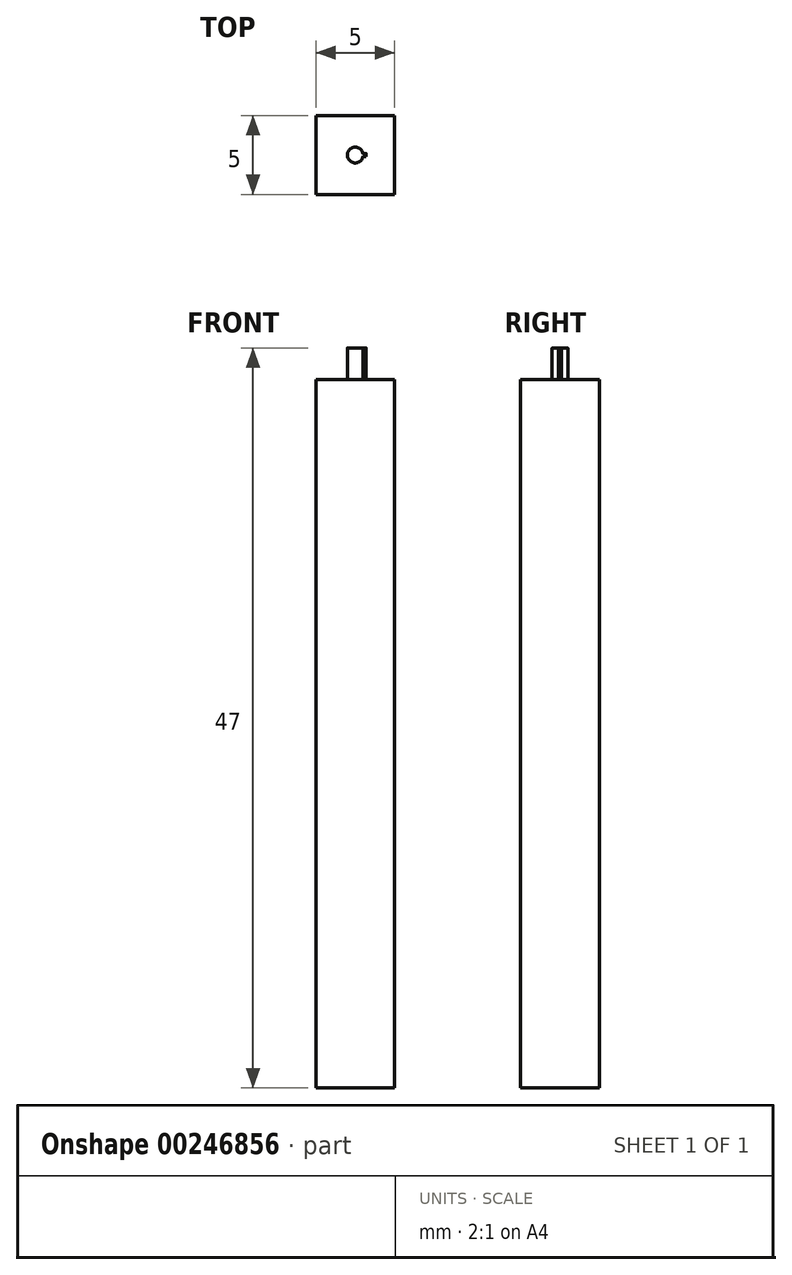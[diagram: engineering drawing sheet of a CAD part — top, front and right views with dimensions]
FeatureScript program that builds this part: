
annotation { "Feature Type Name" : "Feature", "Feature Type Description" : "" }
export const myFeature = defineFeature(function(context is Context, id is Id, definition is map)
    precondition{}
    {
        {
            var Q0;
            Q0=qCreatedBy(makeId("Front.planeOp"),FACE);
            var sketch = newSketch(context, id + "F0", { "sketchPlane" : qUnion([Q0])});
            skLineSegment(sketch, "E0", {"start": v(-2.5, 0) * mm, "end": v(-2.5, 45) * mm});
            skLineSegment(sketch, "E1", {"start": v(-2.5, 45) * mm, "end": v(0, 45) * mm});
            skLineSegment(sketch, "E2.MirrorCS", {"start": v(2.5, 45) * mm, "end": v(0, 45) * mm});
            skLineSegment(sketch, "E3.MirrorCS", {"start": v(2.5, 0) * mm, "end": v(2.5, 45) * mm});
            skLineSegment(sketch, "E4", {"start": v(-2.5, 0) * mm, "end": v(2.5, 0) * mm});
            skLineSegment(sketch, "E5", {"start": v(-2.5, 0) * mm, "end": v(-3, 0) * mm});
            skLineSegment(sketch, "E6.MirrorCS", {"start": v(2.5, 0) * mm, "end": v(3, 0) * mm});
            skSolve(sketch);
        }
        {
            var Q0;
            {var subQ6=sQuery(id+"F0.wireOp",EDGE,"E0");Q0=makeQuery(id+"F0.imprint","IMPRINT",FACE,{"disambiguationData":[TD([[makeQuery(id+"F0.imprint","IMPRINT",EDGE,{"derivedFrom":subQ6}),-1.0]])]});}
            extrude(context, id + "F1", {"entities" : qUnion([Q0]), "depth" : 5 * mm});
        }
        {
            var Q0;
            Q0=makeQuery(id+"F1.opExtrude","SWEPT_FACE",FACE,{"disambiguationData":[OSD([sQuery(id+"F0.wireOp",EDGE,"E1"),sQuery(id+"F0.wireOp",EDGE,"E2.MirrorCS")])]});
            var sketch = newSketch(context, id + "F2", { "sketchPlane" : qUnion([Q0])});
            skCircle(sketch, "E7", {"center": v(0, -2.5) * mm, "radius": 0.5 * mm});
            skPoint(sketch, "E7.centerSnap0", {"position": v(-2.5, -2.5) * mm});
            skLineSegment(sketch, "E8", {"start": v(0.49, -2.4) * mm, "end": v(0.69, -2.4) * mm});
            skLineSegment(sketch, "E9", {"start": v(0.69, -2.4) * mm, "end": v(0.69, -2.5) * mm});
            skLineSegment(sketch, "E10", {"start": v(0.69, -2.5) * mm, "end": v(0.69, -2.6) * mm});
            skLineSegment(sketch, "E11", {"start": v(0.69, -2.6) * mm, "end": v(0.49, -2.6) * mm});
            skSolve(sketch);
        }
        {
            var Q0;
            Q0=makeQuery(id+"F2.imprint","IMPRINT",FACE,{"disambiguationData":[TD([[makeQuery(id+"F2.imprint","IMPRINT",EDGE,{"derivedFrom":sQuery(id+"F2.wireOp",EDGE,"E7")}),1.0]])]});
            extrude(context, id + "F3", {"entities" : qUnion([Q0]), "operationType" : NewBodyOperationType.ADD, "depth" : 2 * mm});
        }
        {
            var Q0;
            {var subQ0=sQuery(id+"F2.wireOp",EDGE,"E8");Q0=makeQuery(id+"F2.imprint","IMPRINT",FACE,{"disambiguationData":[TD([[makeQuery(id+"F2.imprint","IMPRINT",EDGE,{"derivedFrom":subQ0}),-1.0]])]});}
            var Q1;
            Q1=makeQuery(id+"F3.opExtrude","CAP_FACE",FACE,{"disambiguationData":[OSD([sQuery(id+"F2.wireOp",EDGE,"E7")])],"isStart":false});
            extrude(context, id + "F4", {"entities" : qUnion([Q0]), "operationType" : NewBodyOperationType.ADD, "endBound" : BoundingType.UP_TO_SURFACE, "endBoundEntityFace" : qUnion([Q1]), "depth" : 25 * mm});
        }
        {
            var Q0;
            Q0=makeQuery(id+"F4.opExtrude","CAP_EDGE",EDGE,{"disambiguationData":[OSD([sQuery(id+"F2.wireOp",EDGE,"E11")])],"isStart":false});
            var Q1;
            Q1=makeQuery(id+"F4.opExtrude","CAP_EDGE",EDGE,{"disambiguationData":[OSD([sQuery(id+"F2.wireOp",EDGE,"E9"),sQuery(id+"F2.wireOp",EDGE,"E10")])],"isStart":false});
            var Q2;
            Q2=makeQuery(id+"F4.opExtrude","CAP_EDGE",EDGE,{"disambiguationData":[OSD([sQuery(id+"F2.wireOp",EDGE,"E8")])],"isStart":false});
            var Q3;
            Q3=makeQuery(id+"F3.opExtrude","CAP_EDGE",EDGE,{"disambiguationData":[OSD([sQuery(id+"F2.wireOp",EDGE,"E7")])],"isStart":false});
            fillet(context, id + "F5", {"entities" : qUnion([Q0, Q1, Q2, Q3]), "radius" : 0.01 * mm, "tangentPropagation" : true, "allowEdgeOverflow" : false});
        }
    });
